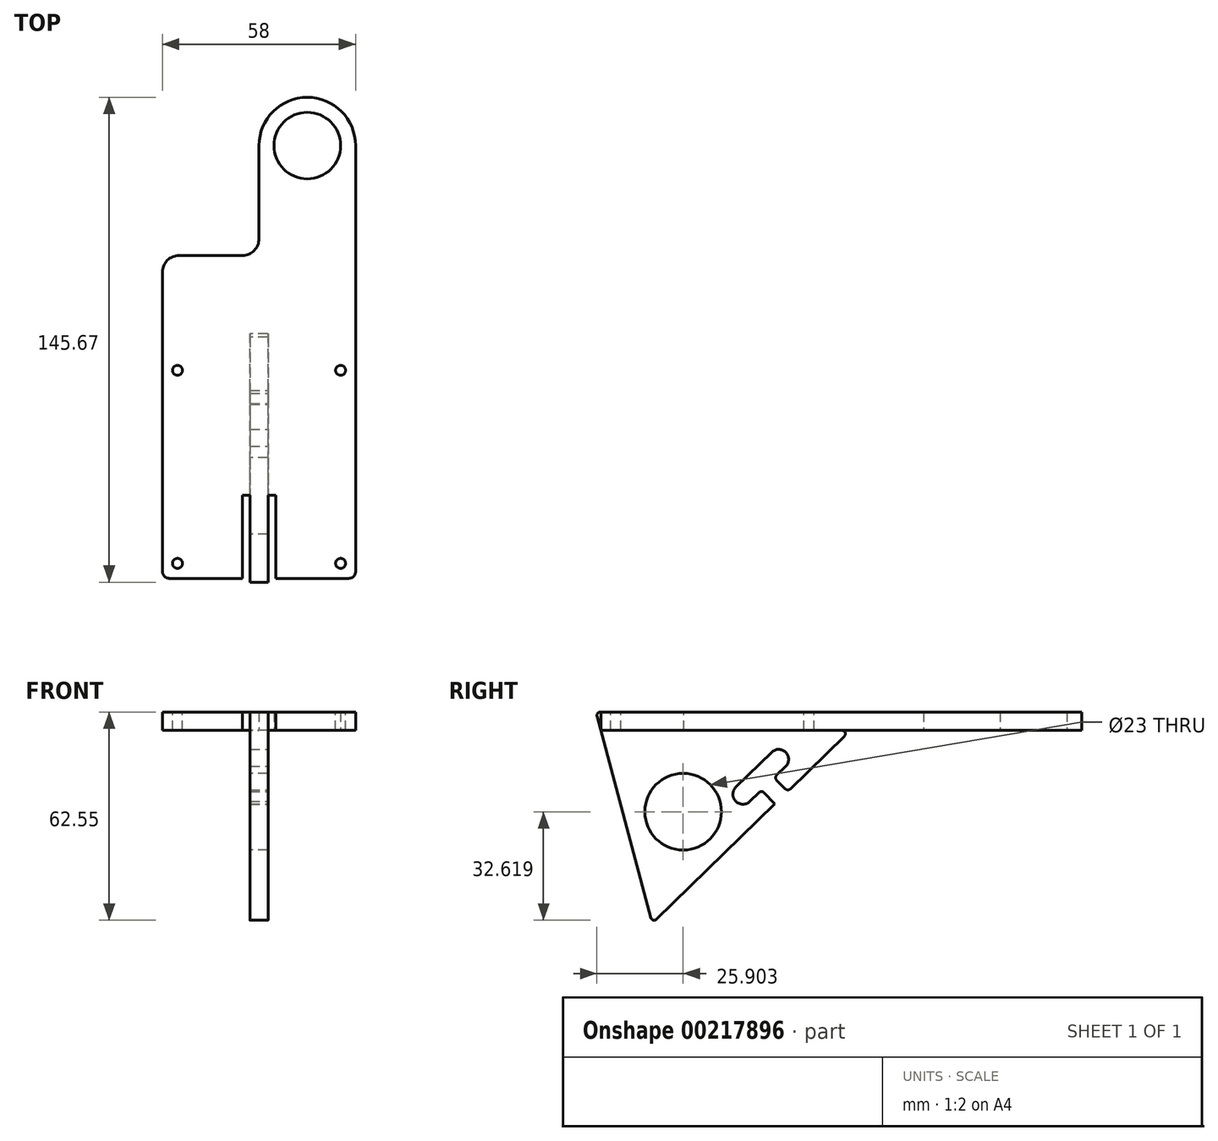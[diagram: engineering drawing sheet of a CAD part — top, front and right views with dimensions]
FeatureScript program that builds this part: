
annotation { "Feature Type Name" : "Feature", "Feature Type Description" : "" }
export const myFeature = defineFeature(function(context is Context, id is Id, definition is map)
    precondition{}
    {
        {
            var Q0;
            Q0=qCreatedBy(makeId("Top.planeOp"),FACE);
            var sketch = newSketch(context, id + "F0", { "sketchPlane" : qUnion([Q0])});
            skLineSegment(sketch, "E0.bottom", {"start": v(27, -48.5) * mm, "end": v(-27, -48.5) * mm});
            skLineSegment(sketch, "E0.right", {"start": v(-29, -46.5) * mm, "end": v(-29, 43.5) * mm});
            skPoint(sketch, "E0.middle", {"position": v(0, 0) * mm});
            skLineSegment(sketch, "E1", {"start": v(29, -46.5) * mm, "end": v(29, 81.5) * mm});
            skArc(sketch, "E2", {"start": v(29, 81.5) * mm, "mid": v(14.5, 96) * mm, "end": v(0, 81.5) * mm});
            skLineSegment(sketch, "E3", {"start": v(0, 81.5) * mm, "end": v(0, 53.5) * mm});
            skLineSegment(sketch, "E4", {"start": v(-5, 48.5) * mm, "end": v(-24, 48.5) * mm});
            skCircle(sketch, "E5", {"center": v(14.5, 81.5) * mm, "radius": 10 * mm});
            skPoint(sketch, "E6.visualSharp", {"position": v(-29, 48.5) * mm});
            skArc(sketch, "E6.filletArc", {"start": v(-24, 48.5) * mm, "mid": v(-27.54, 47.04) * mm, "end": v(-29, 43.5) * mm});
            skPoint(sketch, "E7.visualSharp", {"position": v(0, 48.5) * mm});
            skArc(sketch, "E7.filletArc", {"start": v(-5, 48.5) * mm, "mid": v(-1.46, 49.96) * mm, "end": v(0, 53.5) * mm});
            skPoint(sketch, "E8.visualSharp", {"position": v(-29, -48.5) * mm});
            skArc(sketch, "E8.filletArc", {"start": v(-29, -46.5) * mm, "mid": v(-28.41, -47.91) * mm, "end": v(-27, -48.5) * mm});
            skPoint(sketch, "E9.visualSharp", {"position": v(29, -48.5) * mm});
            skArc(sketch, "E9.filletArc", {"start": v(27, -48.5) * mm, "mid": v(28.41, -47.91) * mm, "end": v(29, -46.5) * mm});
            skSolve(sketch);
        }
        {
            var Q0;
            Q0=makeQuery(id+"F0.imprint","IMPRINT",FACE,{"disambiguationData":[TD([[makeQuery(id+"F0.imprint","IMPRINT",EDGE,{"derivedFrom":sQuery(id+"F0.wireOp",EDGE,"E0.bottom")}),-1.0]])]});
            extrude(context, id + "F1", {"entities" : qUnion([Q0]), "depth" : 5.5 * mm});
        }
        {
            var Q0;
            Q0=makeQuery(id+"F1.opExtrude","CAP_FACE",FACE,{"disambiguationData":[OSD([sQuery(id+"F0.wireOp",EDGE,"E0.bottom"),sQuery(id+"F0.wireOp",EDGE,"E0.right"),sQuery(id+"F0.wireOp",EDGE,"E1"),sQuery(id+"F0.wireOp",EDGE,"E2"),sQuery(id+"F0.wireOp",EDGE,"E3"),sQuery(id+"F0.wireOp",EDGE,"E4"),sQuery(id+"F0.wireOp",EDGE,"E5"),sQuery(id+"F0.wireOp",EDGE,"E6.filletArc"),sQuery(id+"F0.wireOp",EDGE,"E7.filletArc"),sQuery(id+"F0.wireOp",EDGE,"E8.filletArc"),sQuery(id+"F0.wireOp",EDGE,"E9.filletArc")])],"isStart":false});
            var sketch = newSketch(context, id + "F2", { "sketchPlane" : qUnion([Q0])});
            skCircle(sketch, "E10", {"center": v(-24.5, 14) * mm, "radius": 1.5 * mm});
            skCircle(sketch, "E11", {"center": v(24.5, 14) * mm, "radius": 1.5 * mm});
            skCircle(sketch, "E12", {"center": v(24.5, -44) * mm, "radius": 1.5 * mm});
            skCircle(sketch, "E13", {"center": v(-24.5, -44) * mm, "radius": 1.5 * mm});
            skLineSegment(sketch, "E14", {"start": v(-24.5, -44) * mm, "end": v(24.5, -44) * mm, "construction": true});
            skLineSegment(sketch, "E15", {"start": v(24.5, 14) * mm, "end": v(24.5, -44) * mm, "construction": true});
            skLineSegment(sketch, "E16", {"start": v(24.5, 14) * mm, "end": v(-24.5, 14) * mm, "construction": true});
            skLineSegment(sketch, "E17", {"start": v(-24.5, -44) * mm, "end": v(-24.5, 14) * mm, "construction": true});
            skLineSegment(sketch, "E18", {"start": v(0, 14) * mm, "end": v(0, -44) * mm, "construction": true});
            skLineSegment(sketch, "E19", {"start": v(24.5, -44) * mm, "end": v(29, -44) * mm, "construction": true});
            skLineSegment(sketch, "E20", {"start": v(24.5, -44) * mm, "end": v(24.5, -48.5) * mm, "construction": true});
            skSolve(sketch);
        }
        {
            var Q0;
            Q0 = qSketchRegion(id + "F2", true);
            extrude(context, id + "F3", {"entities" : qUnion([Q0]), "operationType" : NewBodyOperationType.REMOVE, "endBound" : BoundingType.UP_TO_NEXT, "oppositeDirection" : true, "depth" : 25 * mm});
        }
        {
            var Q0;
            Q0=makeQuery(id+"F1.opExtrude","CAP_FACE",FACE,{"disambiguationData":[OSD([sQuery(id+"F0.wireOp",EDGE,"E0.bottom"),sQuery(id+"F0.wireOp",EDGE,"E0.right"),sQuery(id+"F0.wireOp",EDGE,"E1"),sQuery(id+"F0.wireOp",EDGE,"E2"),sQuery(id+"F0.wireOp",EDGE,"E3"),sQuery(id+"F0.wireOp",EDGE,"E4"),sQuery(id+"F0.wireOp",EDGE,"E5"),sQuery(id+"F0.wireOp",EDGE,"E6.filletArc"),sQuery(id+"F0.wireOp",EDGE,"E7.filletArc"),sQuery(id+"F0.wireOp",EDGE,"E8.filletArc"),sQuery(id+"F0.wireOp",EDGE,"E9.filletArc")])],"isStart":false});
            var sketch = newSketch(context, id + "F4", { "sketchPlane" : qUnion([Q0])});
            skLineSegment(sketch, "E21.bottom", {"start": v(5, -48.5) * mm, "end": v(-5, -48.5) * mm});
            skLineSegment(sketch, "E21.top", {"start": v(5, -23.58) * mm, "end": v(-5, -23.58) * mm});
            skLineSegment(sketch, "E21.left", {"start": v(5, -48.5) * mm, "end": v(5, -23.58) * mm});
            skLineSegment(sketch, "E21.right", {"start": v(-5, -48.5) * mm, "end": v(-5, -23.58) * mm});
            skLineSegment(sketch, "E22", {"start": v(0, -23.58) * mm, "end": v(0, -48.5) * mm});
            skSolve(sketch);
        }
        {
            var Q0;
            Q0 = qSketchRegion(id + "F4", true);
            extrude(context, id + "F5", {"entities" : qUnion([Q0]), "operationType" : NewBodyOperationType.REMOVE, "endBound" : BoundingType.UP_TO_NEXT, "oppositeDirection" : true, "depth" : 25 * mm});
        }
        {
            var Q0;
            Q0=qCreatedBy(makeId("Right.planeOp"),FACE);
            var sketch = newSketch(context, id + "F6", { "sketchPlane" : qUnion([Q0])});
            skLineSegment(sketch, "E23", {"start": v(-48.5, 0) * mm, "end": v(-32.97, -57.96) * mm});
            skLineSegment(sketch, "E24", {"start": v(-32.97, -57.96) * mm, "end": v(24.67, -1.72) * mm});
            skLineSegment(sketch, "E25", {"start": v(23.97, 0) * mm, "end": v(-23.58, 0) * mm});
            skLineSegment(sketch, "E26", {"start": v(-23.58, 0) * mm, "end": v(-23.58, 5.5) * mm});
            skLineSegment(sketch, "E27", {"start": v(-23.58, 5.5) * mm, "end": v(-48.5, 5.5) * mm});
            skLineSegment(sketch, "E28", {"start": v(-48.5, 0) * mm, "end": v(-49.97, 5.5) * mm});
            skLineSegment(sketch, "E29", {"start": v(-49.97, 5.5) * mm, "end": v(-48.5, 5.5) * mm});
            skCircle(sketch, "E30", {"center": v(-23.77, -24.43) * mm, "radius": 11.5 * mm});
            skLineSegment(sketch, "E31", {"start": v(-40.74, -28.98) * mm, "end": v(-23.77, -24.43) * mm, "construction": true});
            skLineSegment(sketch, "E32", {"start": v(-23.77, -24.43) * mm, "end": v(-11.5, -37) * mm, "construction": true});
            skPoint(sketch, "E33.visualSharp", {"position": v(26.42, 0) * mm});
            skArc(sketch, "E33.filletArc", {"start": v(24.67, -1.72) * mm, "mid": v(24.9, -0.62) * mm, "end": v(23.97, 0) * mm});
            skSolve(sketch);
        }
        {
            var Q0;
            Q0 = qSketchRegion(id + "F6", true);
            extrude(context, id + "F7", {"entities" : qUnion([Q0]), "operationType" : NewBodyOperationType.ADD, "endBound" : BoundingType.SYMMETRIC, "depth" : 5.5 * mm});
        }
        {
            var Q0;
            Q0=makeQuery(id+"F7.opExtrude","SWEPT_EDGE",EDGE,{"disambiguationData":[OSD([sQuery(id+"F6.wireOp",EDGE,"E28"),sQuery(id+"F6.wireOp",EDGE,"E29")])]});
            var Q1;
            Q1=makeQuery(id+"F7.opExtrude","SWEPT_EDGE",EDGE,{"disambiguationData":[OSD([sQuery(id+"F6.wireOp",EDGE,"E23"),sQuery(id+"F6.wireOp",EDGE,"E24")])]});
            fillet(context, id + "F8", {"entities" : qUnion([Q0, Q1]), "radius" : 1 * mm, "tangentPropagation" : true, "allowEdgeOverflow" : false});
        }
        {
            var Q0;
            {var subQ0=sQuery(id+"F6.wireOp",EDGE,"E28");var subQ1=sQuery(id+"F6.wireOp",EDGE,"E23");var subQ2=sQuery(id+"F6.wireOp",EDGE,"E33.filletArc");var subQ3=sQuery(id+"F6.wireOp",EDGE,"E30");var subQ4=sQuery(id+"F6.wireOp",EDGE,"E24");var subQ5=makeQuery(id+"F7.opExtrude","CAP_FACE",FACE,{"disambiguationData":[OSD([subQ1,subQ4,sQuery(id+"F6.wireOp",EDGE,"E25"),sQuery(id+"F6.wireOp",EDGE,"E26"),sQuery(id+"F6.wireOp",EDGE,"E27"),subQ0,sQuery(id+"F6.wireOp",EDGE,"E29"),subQ3,subQ2])],"isStart":false});Q0=makeQuery(id+"F7.boolean.opBoolean","SPLIT",FACE,{"disambiguationData":[TD([makeQuery(id+"F7.opExtrude","SWEPT_FACE",FACE,{"disambiguationData":[OSD([subQ4])]})])],"derivedFrom":subQ5});}
            var sketch = newSketch(context, id + "F9", { "sketchPlane" : qUnion([Q0])});
            skLineSegment(sketch, "E34", {"start": v(-23.77, -24.43) * mm, "end": v(2.39, 1.09) * mm, "construction": true});
            skLineSegment(sketch, "E35", {"start": v(-15.54, -16.4) * mm, "end": v(2.39, 1.09) * mm, "construction": true});
            skLineSegment(sketch, "E36", {"start": v(-6.58, -7.66) * mm, "end": v(5.7, -20.23) * mm, "construction": true});
            skLineSegment(sketch, "E37", {"start": v(-5.8, -19.18) * mm, "end": v(4.93, -8.7) * mm});
            skPoint(sketch, "E38", {"position": v(-0.44, -13.94) * mm});
            skArc(sketch, "E39.0.startCap", {"start": v(-3.69, -21.3) * mm, "mid": v(-7.94, -21.29) * mm, "end": v(-7.9, -17.03) * mm});
            skArc(sketch, "E39.0.endCap", {"start": v(2.83, -6.56) * mm, "mid": v(7.06, -6.6) * mm, "end": v(7.05, -10.83) * mm});
            skLineSegment(sketch, "E39.0.left", {"start": v(-7.9, -17.03) * mm, "end": v(2.83, -6.56) * mm});
            skLineSegment(sketch, "E40", {"start": v(-3.69, -21.3) * mm, "end": v(-0.23, -17.93) * mm});
            skLineSegment(sketch, "E41", {"start": v(-0.23, -17.93) * mm, "end": v(3.8, -22.07) * mm});
            skLineSegment(sketch, "E42", {"start": v(3.8, -22.07) * mm, "end": v(7.68, -18.29) * mm});
            skLineSegment(sketch, "E43", {"start": v(7.68, -18.29) * mm, "end": v(3.6, -14.2) * mm});
            skLineSegment(sketch, "E44", {"start": v(3.6, -14.2) * mm, "end": v(7.05, -10.83) * mm});
            skSolve(sketch);
        }
        {
            var Q0;
            Q0 = qSketchRegion(id + "F9", true);
            extrude(context, id + "F10", {"entities" : qUnion([Q0]), "operationType" : NewBodyOperationType.REMOVE, "endBound" : BoundingType.UP_TO_NEXT, "oppositeDirection" : true, "depth" : 25 * mm});
        }
        {
            var Q0;
            Q0=makeQuery(id+"F10.boolean.opBoolean","COPY",EDGE,{"derivedFrom":makeQuery(id+"F10.opExtrude","SWEPT_EDGE",EDGE,{"disambiguationData":[OSD([sQuery(id+"F9.wireOp",EDGE,"E40"),sQuery(id+"F9.wireOp",EDGE,"E41")])]})});
            var Q1;
            Q1=makeQuery(id+"F10.boolean.opBoolean","COPY",EDGE,{"derivedFrom":makeQuery(id+"F10.opExtrude","SWEPT_EDGE",EDGE,{"disambiguationData":[OSD([sQuery(id+"F9.wireOp",EDGE,"E43"),sQuery(id+"F9.wireOp",EDGE,"E44")])]})});
            var Q2;
            Q2=makeQuery(id+"F10.boolean.opBoolean","COPY",EDGE,{"derivedFrom":makeQuery(id+"F10.opExtrude","SWEPT_EDGE",EDGE,{"disambiguationData":[OSD([sQuery(id+"F6.wireOp",EDGE,"E24"),sQuery(id+"F9.wireOp",EDGE,"E42"),sQuery(id+"F9.wireOp",EDGE,"E43")])]})});
            var Q3;
            Q3=makeQuery(id+"F10.boolean.opBoolean","COPY",EDGE,{"derivedFrom":makeQuery(id+"F10.opExtrude","SWEPT_EDGE",EDGE,{"disambiguationData":[OSD([sQuery(id+"F6.wireOp",EDGE,"E24"),sQuery(id+"F9.wireOp",EDGE,"E41"),sQuery(id+"F9.wireOp",EDGE,"E42")])]})});
            fillet(context, id + "F11", {"entities" : qUnion([Q0, Q1, Q2, Q3]), "radius" : 1 * mm, "tangentPropagation" : true, "allowEdgeOverflow" : false});
        }
    });
